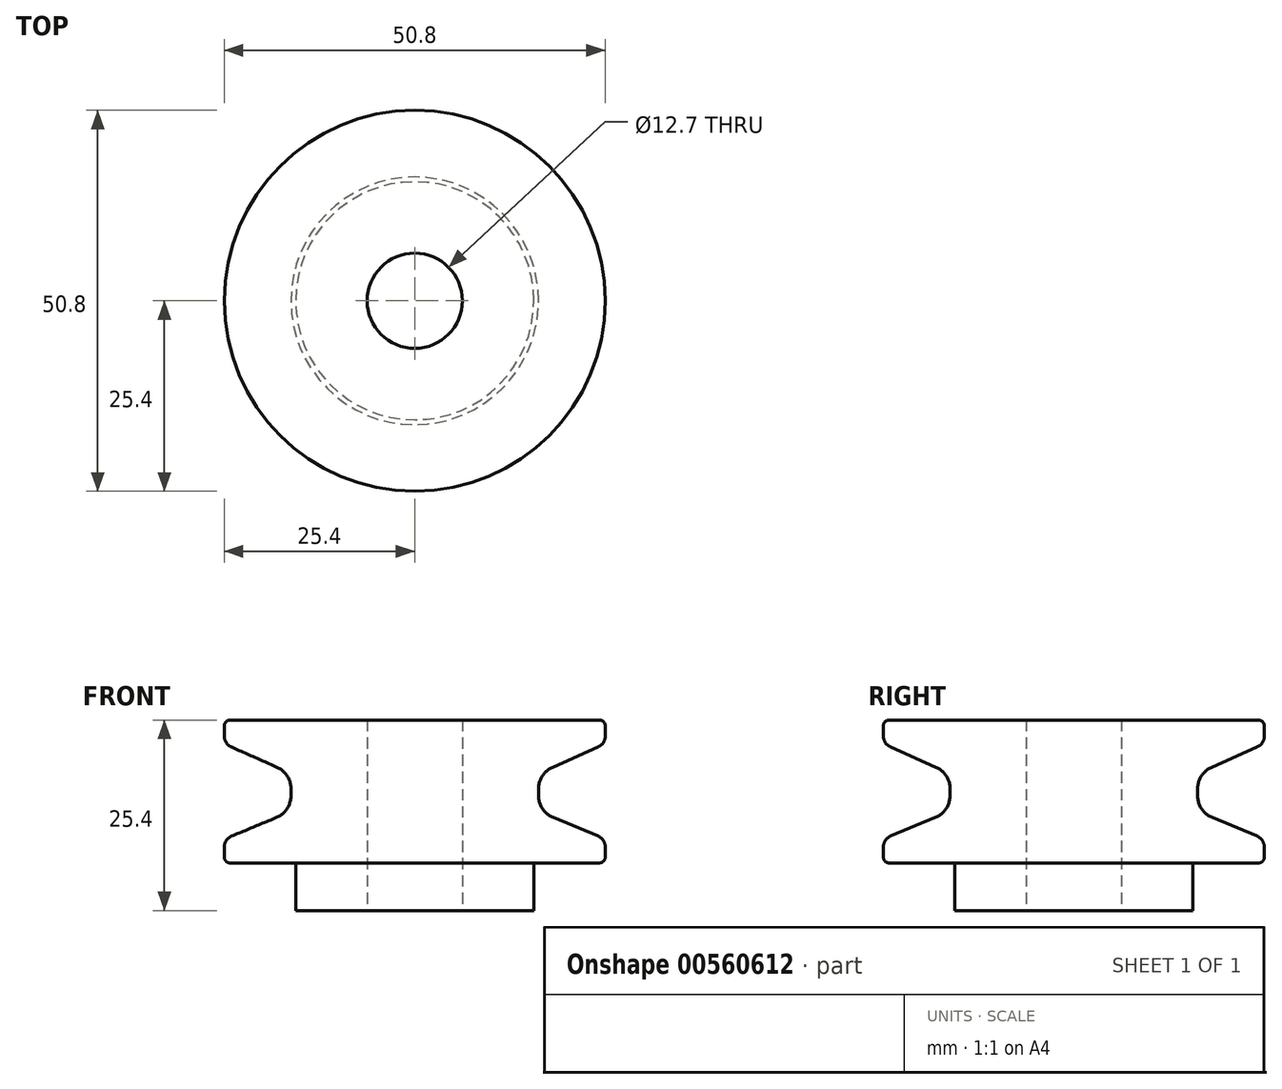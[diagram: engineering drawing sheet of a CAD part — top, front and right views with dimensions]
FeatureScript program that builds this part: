
annotation { "Feature Type Name" : "Feature", "Feature Type Description" : "" }
export const myFeature = defineFeature(function(context is Context, id is Id, definition is map)
    precondition{}
    {
        {
            var Q0;
            Q0=qCreatedBy(makeId("Front.planeOp"),FACE);
            var sketch = newSketch(context, id + "F0", { "sketchPlane" : qUnion([Q0])});
            skLineSegment(sketch, "E0.top", {"start": v(-6.35, 20.85) * mm, "end": v(-24.64, 20.85) * mm});
            skLineSegment(sketch, "E0.left", {"start": v(0, -20.74) * mm, "end": v(0, 20.85) * mm});
            skLineSegment(sketch, "E1", {"start": v(-25.4, 20.09) * mm, "end": v(-25.4, 18.7) * mm});
            skLineSegment(sketch, "E2", {"start": v(-25.4, 3.92) * mm, "end": v(-25.4, 2.56) * mm});
            skLineSegment(sketch, "E3", {"start": v(-24.64, 1.8) * mm, "end": v(-15.88, 1.8) * mm});
            skLineSegment(sketch, "E4", {"start": v(-15.88, 1.8) * mm, "end": v(-15.88, -4.55) * mm});
            skLineSegment(sketch, "E5", {"start": v(-15.88, -4.55) * mm, "end": v(-6.35, -4.55) * mm});
            skLineSegment(sketch, "E6", {"start": v(-6.35, 20.85) * mm, "end": v(-6.35, -4.55) * mm});
            skLineSegment(sketch, "E7", {"start": v(-24.46, 17.26) * mm, "end": v(-18.4, 14.57) * mm});
            skLineSegment(sketch, "E8", {"start": v(-16.51, 11.67) * mm, "end": v(-16.51, 10.78) * mm});
            skLineSegment(sketch, "E9", {"start": v(-18.47, 7.85) * mm, "end": v(-24.43, 5.38) * mm});
            skPoint(sketch, "E10.visualSharp", {"position": v(-16.51, 13.74) * mm});
            skArc(sketch, "E10.filletArc", {"start": v(-16.51, 11.67) * mm, "mid": v(-17.02, 13.4) * mm, "end": v(-18.4, 14.57) * mm});
            skPoint(sketch, "E11.visualSharp", {"position": v(-16.51, 8.66) * mm});
            skArc(sketch, "E11.filletArc", {"start": v(-18.47, 7.85) * mm, "mid": v(-17.05, 9.01) * mm, "end": v(-16.5, 10.78) * mm});
            skPoint(sketch, "E12.visualSharp", {"position": v(-25.4, 17.67) * mm});
            skArc(sketch, "E12.filletArc", {"start": v(-25.4, 18.7) * mm, "mid": v(-25.15, 17.84) * mm, "end": v(-24.46, 17.26) * mm});
            skPoint(sketch, "E13.visualSharp", {"position": v(-25.4, 4.97) * mm});
            skArc(sketch, "E13.filletArc", {"start": v(-24.43, 5.38) * mm, "mid": v(-25.13, 4.8) * mm, "end": v(-25.4, 3.92) * mm});
            skPoint(sketch, "E14.visualSharp", {"position": v(-25.4, 20.85) * mm});
            skArc(sketch, "E14.filletArc", {"start": v(-24.64, 20.85) * mm, "mid": v(-25.18, 20.63) * mm, "end": v(-25.4, 20.09) * mm});
            skPoint(sketch, "E15.visualSharp", {"position": v(-25.4, 1.8) * mm});
            skArc(sketch, "E15.filletArc", {"start": v(-25.4, 2.56) * mm, "mid": v(-25.18, 2.02) * mm, "end": v(-24.64, 1.8) * mm});
            skSolve(sketch);
        }
        {
            var Q0;
            Q0=makeQuery(id+"F0.imprint","IMPRINT",FACE,{"disambiguationData":[TD([[makeQuery(id+"F0.imprint","IMPRINT",EDGE,{"derivedFrom":sQuery(id+"F0.wireOp",EDGE,"E0.top")}),1.0]])]});
            var Q1;
            Q1=sQuery(id+"F0.wireOp",EDGE,"E0.left");
            revolve(context, id + "F1", {"entities" : qUnion([Q0]), "axis" : qUnion([Q1]), "revolveType" : RevolveType.FULL});
        }
    });
